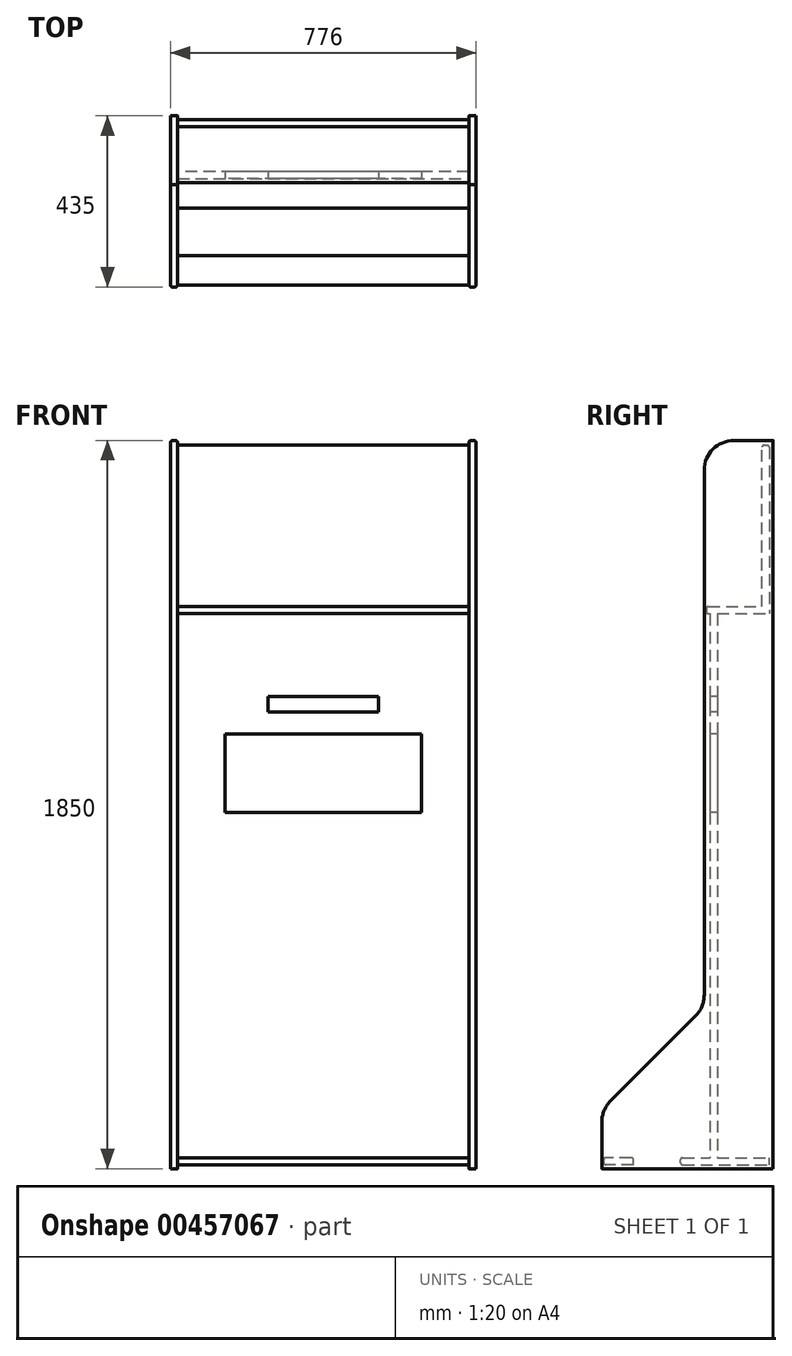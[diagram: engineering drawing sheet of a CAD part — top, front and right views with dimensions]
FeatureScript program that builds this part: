
annotation { "Feature Type Name" : "Feature", "Feature Type Description" : "" }
export const myFeature = defineFeature(function(context is Context, id is Id, definition is map)
    precondition{}
    {
        {
            var Q0;
            Q0=qCreatedBy(makeId("Right.planeOp"),FACE);
            var sketch = newSketch(context, id + "F0", { "sketchPlane" : qUnion([Q0])});
            skLineSegment(sketch, "E0", {"start": v(0, 0) * mm, "end": v(0, 1850) * mm});
            skLineSegment(sketch, "E1", {"start": v(0, 1850) * mm, "end": v(-100, 1850) * mm});
            skLineSegment(sketch, "E2", {"start": v(-175, 1775) * mm, "end": v(-175, 441.07) * mm});
            skLineSegment(sketch, "E3", {"start": v(-196.97, 388.03) * mm, "end": v(-413.03, 171.97) * mm});
            skLineSegment(sketch, "E4", {"start": v(-435, 118.93) * mm, "end": v(-435, 0) * mm});
            skLineSegment(sketch, "E5", {"start": v(-435, 0) * mm, "end": v(0, 0) * mm});
            skPoint(sketch, "E6.visualSharp", {"position": v(-175, 1850) * mm});
            skArc(sketch, "E6.filletArc", {"start": v(-100, 1850) * mm, "mid": v(-153.03, 1828.03) * mm, "end": v(-175, 1775) * mm});
            skPoint(sketch, "E7.visualSharp", {"position": v(-175, 410) * mm});
            skArc(sketch, "E7.filletArc", {"start": v(-196.97, 388.03) * mm, "mid": v(-180.7, 412.36) * mm, "end": v(-175, 441.07) * mm});
            skPoint(sketch, "E8.visualSharp", {"position": v(-435, 150) * mm});
            skArc(sketch, "E8.filletArc", {"start": v(-413.03, 171.97) * mm, "mid": v(-429.3, 147.64) * mm, "end": v(-435, 118.93) * mm});
            skSolve(sketch);
        }
        {
            var Q0;
            Q0 = qSketchRegion(id + "F0", true);
            extrude(context, id + "F1", {"entities" : qUnion([Q0]), "depth" : 18 * mm});
        }
        {
            var Q0;
            Q0=makeQuery(id+"F1.opExtrude","SWEPT_FACE",FACE,{"disambiguationData":[OSD([sQuery(id+"F0.wireOp",EDGE,"E2")])]});
            cPlane(context, id + "F2", {"entities" : qUnion([Q0]), "cplaneType" : CPlaneType.OFFSET, "offset" : 15 * mm, "oppositeDirection" : true, "width" : 150 * mm, "height" : 150 * mm});
        }
        {
            var Q0;
            Q0=qCreatedBy(id+"F2.planeOp",FACE);
            var sketch = newSketch(context, id + "F3", { "sketchPlane" : qUnion([Q0])});
            skLineSegment(sketch, "E9", {"start": v(758, 1410) * mm, "end": v(758, 28) * mm});
            skLineSegment(sketch, "E10", {"start": v(758, 28) * mm, "end": v(18, 28) * mm});
            skLineSegment(sketch, "E11", {"start": v(388, 1410) * mm, "end": v(388, 1180) * mm, "construction": true});
            skLineSegment(sketch, "E12", {"start": v(388, 1180) * mm, "end": v(388, 1005) * mm, "construction": true});
            skLineSegment(sketch, "E13.bottom", {"start": v(528, 1200) * mm, "end": v(248, 1200) * mm});
            skLineSegment(sketch, "E13.top", {"start": v(528, 1160) * mm, "end": v(248, 1160) * mm});
            skLineSegment(sketch, "E13.left", {"start": v(528, 1200) * mm, "end": v(528, 1160) * mm});
            skLineSegment(sketch, "E13.right", {"start": v(248, 1200) * mm, "end": v(248, 1160) * mm});
            skPoint(sketch, "E13.middle", {"position": v(388, 1180) * mm});
            skLineSegment(sketch, "E14.bottom", {"start": v(638, 1105) * mm, "end": v(138, 1105) * mm});
            skLineSegment(sketch, "E14.top", {"start": v(638, 905) * mm, "end": v(138, 905) * mm});
            skLineSegment(sketch, "E14.left", {"start": v(638, 1105) * mm, "end": v(638, 905) * mm});
            skLineSegment(sketch, "E14.right", {"start": v(138, 1105) * mm, "end": v(138, 905) * mm});
            skPoint(sketch, "E14.middle", {"position": v(388, 1005) * mm});
            skLineSegment(sketch, "E15", {"start": v(18, 28) * mm, "end": v(18, 1410) * mm});
            skLineSegment(sketch, "E16", {"start": v(18, 1410) * mm, "end": v(758, 1410) * mm});
            skSolve(sketch);
        }
        {
            var Q0;
            Q0 = qSketchRegion(id + "F3", true);
            extrude(context, id + "F4", {"entities" : qUnion([Q0]), "operationType" : NewBodyOperationType.ADD, "oppositeDirection" : true, "depth" : 18 * mm});
        }
        {
            var Q0;
            Q0=makeQuery(id+"F4.opExtrude","SWEPT_FACE",FACE,{"disambiguationData":[OSD([sQuery(id+"F3.wireOp",EDGE,"E9")])]});
            cPlane(context, id + "F5", {"entities" : qUnion([Q0]), "cplaneType" : CPlaneType.OFFSET, "offset" : 0 * mm, "width" : 150 * mm, "height" : 150 * mm});
        }
        {
            var Q0;
            Q0=qCreatedBy(id+"F5.planeOp",FACE);
            var sketch = newSketch(context, id + "F6", { "sketchPlane" : qUnion([Q0])});
            skLineSegment(sketch, "E17", {"start": v(0, 0) * mm, "end": v(-435, 0) * mm});
            skLineSegment(sketch, "E18", {"start": v(-435, 0) * mm, "end": v(-435, 118.93) * mm});
            skLineSegment(sketch, "E19", {"start": v(-413.03, 171.97) * mm, "end": v(-196.97, 388.03) * mm});
            skLineSegment(sketch, "E20", {"start": v(-175, 441.07) * mm, "end": v(-175, 1775) * mm});
            skLineSegment(sketch, "E21", {"start": v(-100, 1850) * mm, "end": v(0, 1850) * mm});
            skLineSegment(sketch, "E22", {"start": v(0, 1850) * mm, "end": v(0, 0) * mm});
            skPoint(sketch, "E23.visualSharp", {"position": v(-175, 410) * mm});
            skArc(sketch, "E23.filletArc", {"start": v(-196.97, 388.03) * mm, "mid": v(-180.7, 412.36) * mm, "end": v(-175, 441.07) * mm});
            skPoint(sketch, "E24.visualSharp", {"position": v(-435, 150) * mm});
            skArc(sketch, "E24.filletArc", {"start": v(-413.03, 171.97) * mm, "mid": v(-429.3, 147.64) * mm, "end": v(-435, 118.93) * mm});
            skPoint(sketch, "E25.visualSharp", {"position": v(-175, 1850) * mm});
            skArc(sketch, "E25.filletArc", {"start": v(-100, 1850) * mm, "mid": v(-153.03, 1828.03) * mm, "end": v(-175, 1775) * mm});
            skSolve(sketch);
        }
        {
            var Q0;
            Q0 = qSketchRegion(id + "F6", true);
            extrude(context, id + "F7", {"entities" : qUnion([Q0]), "operationType" : NewBodyOperationType.ADD, "depth" : 18 * mm});
        }
        {
            var Q0;
            Q0=makeQuery(id+"F4.opExtrude","SWEPT_FACE",FACE,{"disambiguationData":[OSD([sQuery(id+"F3.wireOp",EDGE,"E16")])]});
            cPlane(context, id + "F8", {"entities" : qUnion([Q0]), "cplaneType" : CPlaneType.OFFSET, "offset" : 0 * mm, "width" : 150 * mm, "height" : 150 * mm});
        }
        {
            var Q0;
            Q0=qCreatedBy(id+"F8.planeOp",FACE);
            var sketch = newSketch(context, id + "F9", { "sketchPlane" : qUnion([Q0])});
            skLineSegment(sketch, "E26.bottom", {"start": v(18, -170) * mm, "end": v(758, -170) * mm});
            skLineSegment(sketch, "E26.top", {"start": v(18, -10) * mm, "end": v(758, -10) * mm});
            skLineSegment(sketch, "E26.left", {"start": v(18, -170) * mm, "end": v(18, -10) * mm});
            skLineSegment(sketch, "E26.right", {"start": v(758, -170) * mm, "end": v(758, -10) * mm});
            skSolve(sketch);
        }
        {
            var Q0;
            Q0 = qSketchRegion(id + "F9", true);
            extrude(context, id + "F10", {"entities" : qUnion([Q0]), "operationType" : NewBodyOperationType.ADD, "depth" : 18 * mm});
        }
        {
            var Q0;
            Q0=makeQuery(id+"F10.opExtrude","SWEPT_FACE",FACE,{"disambiguationData":[OSD([sQuery(id+"F9.wireOp",EDGE,"E26.top")])]});
            cPlane(context, id + "F11", {"entities" : qUnion([Q0]), "cplaneType" : CPlaneType.OFFSET, "offset" : 0 * mm, "width" : 150 * mm, "height" : 150 * mm});
        }
        {
            var Q0;
            Q0=qCreatedBy(id+"F11.planeOp",FACE);
            var sketch = newSketch(context, id + "F12", { "sketchPlane" : qUnion([Q0])});
            skLineSegment(sketch, "E27", {"start": v(-758, 1428) * mm, "end": v(-758, 1838) * mm});
            skLineSegment(sketch, "E28", {"start": v(-758, 1838) * mm, "end": v(-18, 1838) * mm});
            skLineSegment(sketch, "E29", {"start": v(-18, 1838) * mm, "end": v(-18, 1428) * mm});
            skLineSegment(sketch, "E30", {"start": v(-758, 1428) * mm, "end": v(-18, 1428) * mm});
            skSolve(sketch);
        }
        {
            var Q0;
            Q0 = qSketchRegion(id + "F12", true);
            extrude(context, id + "F13", {"entities" : qUnion([Q0]), "operationType" : NewBodyOperationType.ADD, "oppositeDirection" : true, "depth" : 18 * mm});
        }
        {
            var Q0;
            Q0=makeQuery(id+"F4.opExtrude","SWEPT_FACE",FACE,{"disambiguationData":[OSD([sQuery(id+"F3.wireOp",EDGE,"E10")])]});
            cPlane(context, id + "F14", {"entities" : qUnion([Q0]), "cplaneType" : CPlaneType.OFFSET, "offset" : 0 * mm, "width" : 150 * mm, "height" : 150 * mm});
        }
        {
            var Q0;
            Q0=qCreatedBy(id+"F14.planeOp",FACE);
            var sketch = newSketch(context, id + "F15", { "sketchPlane" : qUnion([Q0])});
            skLineSegment(sketch, "E31", {"start": v(758, 10) * mm, "end": v(18, 10) * mm});
            skLineSegment(sketch, "E32", {"start": v(18, 10) * mm, "end": v(18, 235) * mm});
            skLineSegment(sketch, "E33", {"start": v(18, 235) * mm, "end": v(758, 235) * mm});
            skLineSegment(sketch, "E34", {"start": v(758, 235) * mm, "end": v(758, 10) * mm});
            skLineSegment(sketch, "E35.bottom", {"start": v(758, 355) * mm, "end": v(18, 355) * mm});
            skLineSegment(sketch, "E35.top", {"start": v(758, 430) * mm, "end": v(18, 430) * mm});
            skLineSegment(sketch, "E35.left", {"start": v(758, 355) * mm, "end": v(758, 430) * mm});
            skLineSegment(sketch, "E35.right", {"start": v(18, 355) * mm, "end": v(18, 430) * mm});
            skSolve(sketch);
        }
        {
            var Q0;
            Q0 = qSketchRegion(id + "F15", true);
            extrude(context, id + "F16", {"entities" : qUnion([Q0]), "operationType" : NewBodyOperationType.ADD, "depth" : 18 * mm});
        }
        {
            var Q0;
            Q0=makeQuery(id+"F10.opExtrude","CAP_EDGE",EDGE,{"disambiguationData":[OSD([sQuery(id+"F9.wireOp",EDGE,"E26.bottom")])],"isStart":false});
            var Q1;
            Q1=makeQuery(id+"F10.opExtrude","CAP_EDGE",EDGE,{"disambiguationData":[OSD([sQuery(id+"F9.wireOp",EDGE,"E26.bottom")])],"isStart":true});
            var Q2;
            Q2=makeQuery(id+"F7.opExtrude","CAP_EDGE",EDGE,{"disambiguationData":[OSD([sQuery(id+"F6.wireOp",EDGE,"E20")])],"isStart":true});
            var Q3;
            Q3=makeQuery(id+"F7.opExtrude","CAP_EDGE",EDGE,{"disambiguationData":[OSD([sQuery(id+"F6.wireOp",EDGE,"E20")])],"isStart":false});
            var Q4;
            Q4=makeQuery(id+"F13.opExtrude","CAP_EDGE",EDGE,{"disambiguationData":[OSD([sQuery(id+"F12.wireOp",EDGE,"E28")])],"isStart":false});
            var Q5;
            Q5=makeQuery(id+"F13.opExtrude","CAP_EDGE",EDGE,{"disambiguationData":[OSD([sQuery(id+"F12.wireOp",EDGE,"E28")])],"isStart":true});
            var Q6;
            Q6=makeQuery(id+"F1.opExtrude","CAP_EDGE",EDGE,{"disambiguationData":[OSD([sQuery(id+"F0.wireOp",EDGE,"E1")])],"isStart":false});
            var Q7;
            Q7=makeQuery(id+"F1.opExtrude","CAP_EDGE",EDGE,{"disambiguationData":[OSD([sQuery(id+"F0.wireOp",EDGE,"E1")])],"isStart":true});
            var Q8;
            Q8=makeQuery(id+"F16.opExtrude","CAP_EDGE",EDGE,{"disambiguationData":[OSD([sQuery(id+"F15.wireOp",EDGE,"E33")])],"isStart":true});
            var Q9;
            Q9=makeQuery(id+"F16.opExtrude","CAP_EDGE",EDGE,{"disambiguationData":[OSD([sQuery(id+"F15.wireOp",EDGE,"E35.bottom")])],"isStart":true});
            var Q10;
            Q10=makeQuery(id+"F16.opExtrude","CAP_EDGE",EDGE,{"disambiguationData":[OSD([sQuery(id+"F15.wireOp",EDGE,"E35.top")])],"isStart":true});
            var Q11;
            Q11=makeQuery(id+"F16.opExtrude","CAP_EDGE",EDGE,{"disambiguationData":[OSD([sQuery(id+"F15.wireOp",EDGE,"E35.top")])],"isStart":false});
            var Q12;
            Q12=makeQuery(id+"F16.opExtrude","CAP_EDGE",EDGE,{"disambiguationData":[OSD([sQuery(id+"F15.wireOp",EDGE,"E33")])],"isStart":false});
            fillet(context, id + "F17", {"entities" : qUnion([Q0, Q1, Q2, Q3, Q4, Q5, Q6, Q7, Q8, Q9, Q10, Q11, Q12]), "radius" : 5 * mm, "tangentPropagation" : true, "allowEdgeOverflow" : false});
        }
    });
